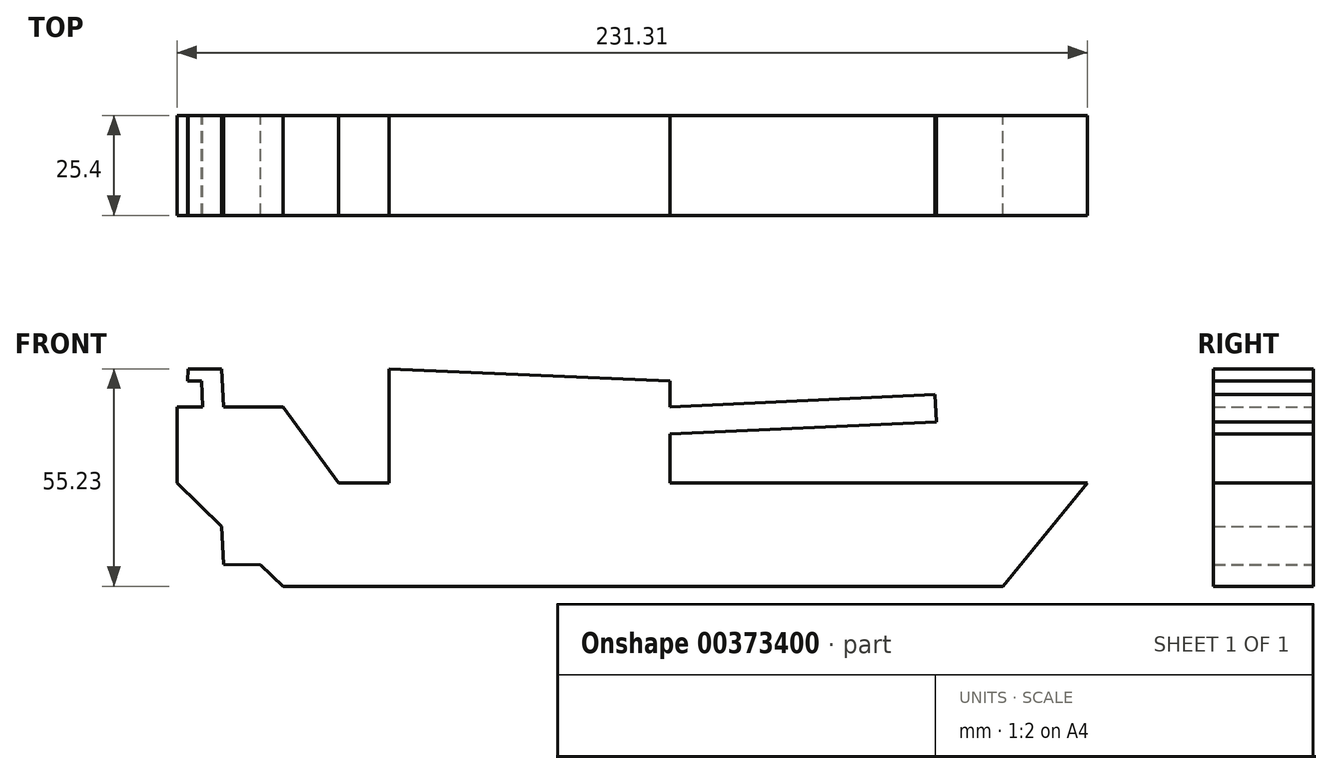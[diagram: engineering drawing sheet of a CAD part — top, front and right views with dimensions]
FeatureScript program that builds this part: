
annotation { "Feature Type Name" : "Feature", "Feature Type Description" : "" }
export const myFeature = defineFeature(function(context is Context, id is Id, definition is map)
    precondition{}
    {
        {
            var Q0;
            Q0=qCreatedBy(makeId("Front.planeOp"),FACE);
            var sketch = newSketch(context, id + "F0", { "sketchPlane" : qUnion([Q0])});
            skLineSegment(sketch, "E0", {"start": v(-127.4, -64.21) * mm, "end": v(55.58, -64.21) * mm});
            skLineSegment(sketch, "E1", {"start": v(55.58, -64.21) * mm, "end": v(76.99, -37.98) * mm});
            skLineSegment(sketch, "E2", {"start": v(76.99, -37.98) * mm, "end": v(-154.32, -37.98) * mm});
            skLineSegment(sketch, "E3", {"start": v(-154.32, -37.98) * mm, "end": v(-127.4, -64.21) * mm});
            skLineSegment(sketch, "E4", {"start": v(-154.32, -37.98) * mm, "end": v(-154.32, -18.64) * mm});
            skLineSegment(sketch, "E5", {"start": v(-154.32, -18.64) * mm, "end": v(-127.4, -18.64) * mm});
            skLineSegment(sketch, "E6", {"start": v(-127.4, -18.64) * mm, "end": v(-113.24, -37.98) * mm});
            skLineSegment(sketch, "E7", {"start": v(-100.46, -8.98) * mm, "end": v(-100.46, -37.98) * mm});
            skLineSegment(sketch, "E8", {"start": v(-100.46, -37.98) * mm, "end": v(-29, -37.98) * mm});
            skLineSegment(sketch, "E9", {"start": v(-29, -37.98) * mm, "end": v(-29, -12.08) * mm});
            skLineSegment(sketch, "E10", {"start": v(-29, -12.08) * mm, "end": v(-100.46, -8.98) * mm});
            skLineSegment(sketch, "E11", {"start": v(-29, -18.64) * mm, "end": v(38.32, -15.54) * mm});
            skLineSegment(sketch, "E12", {"start": v(38.32, -15.54) * mm, "end": v(38.64, -22.43) * mm});
            skLineSegment(sketch, "E13", {"start": v(38.64, -22.43) * mm, "end": v(-29, -25.55) * mm});
            skLineSegment(sketch, "E14", {"start": v(-147.76, -18.64) * mm, "end": v(-148.06, -12.08) * mm});
            skLineSegment(sketch, "E15", {"start": v(-148.06, -12.08) * mm, "end": v(-151.56, -12.08) * mm});
            skLineSegment(sketch, "E16", {"start": v(-151.56, -12.08) * mm, "end": v(-151.42, -8.98) * mm});
            skLineSegment(sketch, "E17", {"start": v(-151.42, -8.98) * mm, "end": v(-142.93, -8.98) * mm});
            skLineSegment(sketch, "E18", {"start": v(-142.93, -8.98) * mm, "end": v(-142.48, -18.64) * mm});
            skLineSegment(sketch, "E19", {"start": v(-133, -58.75) * mm, "end": v(-142.48, -58.69) * mm});
            skLineSegment(sketch, "E20", {"start": v(-142.48, -58.69) * mm, "end": v(-142.92, -49.08) * mm});
            skLineSegment(sketch, "E21", {"start": v(-142.92, -49.08) * mm, "end": v(-142.07, -67.66) * mm});
            skSolve(sketch);
        }
        {
            var Q0;
            {var subQ4=sQuery(id+"F0.wireOp",EDGE,"E0");Q0=makeQuery(id+"F0.imprint","IMPRINT",FACE,{"disambiguationData":[TD([[makeQuery(id+"F0.imprint","IMPRINT",EDGE,{"derivedFrom":subQ4}),1.0]])]});}
            var Q1;
            Q1=makeQuery(id+"F0.imprint","IMPRINT",FACE,{"disambiguationData":[TD([[makeQuery(id+"F0.imprint","IMPRINT",EDGE,{"derivedFrom":sQuery(id+"F0.wireOp",EDGE,"E7")}),1.0]])]});
            var Q2;
            {var subQ3=sQuery(id+"F0.wireOp",EDGE,"E4");Q2=makeQuery(id+"F0.imprint","IMPRINT",FACE,{"disambiguationData":[TD([[makeQuery(id+"F0.imprint","IMPRINT",EDGE,{"derivedFrom":subQ3}),-1.0]])]});}
            var Q3;
            {var subQ0=sQuery(id+"F0.wireOp",EDGE,"E14");Q3=makeQuery(id+"F0.imprint","IMPRINT",FACE,{"disambiguationData":[TD([[makeQuery(id+"F0.imprint","IMPRINT",EDGE,{"derivedFrom":subQ0}),-1.0]])]});}
            var Q4;
            {var subQ0=sQuery(id+"F0.wireOp",EDGE,"E19");Q4=makeQuery(id+"F0.imprint","IMPRINT",FACE,{"disambiguationData":[TD([[makeQuery(id+"F0.imprint","IMPRINT",EDGE,{"derivedFrom":subQ0}),-1.0]])]});}
            var Q5;
            {var subQ0=sQuery(id+"F0.wireOp",EDGE,"E11");Q5=makeQuery(id+"F0.imprint","IMPRINT",FACE,{"disambiguationData":[TD([[makeQuery(id+"F0.imprint","IMPRINT",EDGE,{"derivedFrom":subQ0}),-1.0]])]});}
            extrude(context, id + "F1", {"entities" : qUnion([Q0, Q1, Q2, Q3, Q4, Q5]), "depth" : 25.4 * mm});
        }
    });
